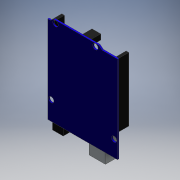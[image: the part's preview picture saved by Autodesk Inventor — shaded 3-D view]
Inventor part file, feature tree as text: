
AUTODESK INVENTOR PART (.ipt)
format: ipt  version: 2016 (Build 200138000, 138)  size: 185,856 bytes
history: native  units: mm
features: sketch x7, extrude x6, other x1
ambient origin geometry x8: Origin, YZ Plane, XZ Plane, XY Plane, X Axis, Y Axis, Z Axis, Center Point
bodies: Body1 (feature_tree)
feature tree (14):
  other  "Sólido1"
  extrude  "Extrusión1"  Depth=8.45mm TaperAngle=0.0deg
  extrude  "Extrusión2"  Depth=10.0mm TaperAngle=0.0deg
  extrude  "Extrusión3"  Depth=12.0mm TaperAngle=0.0deg
  extrude  "Extrusión4"  [1 undecoded]
  extrude  "Extrusión5"  [1 undecoded]
  extrude  "Extrusión6"  [1 undecoded]
  sketch  "Boceto7"
  sketch  "Boceto1"  dims[d25=1.0mm d26=0.0mm d39=8.45mm d40=0.0mm]
  sketch  "Boceto2"  dims[d45=8.0mm d46=0.0mm d51=10.0mm d52=0.0mm]
  sketch  "Boceto3"  dims[d57=10.0mm d58=0.0mm d60=12.0mm d61=0.0mm]
  sketch  "Boceto4"
  sketch  "Boceto5"
  sketch  "Boceto6"
note: 3 required parameter values undecoded (feature->parameter linkage not recoverable at this tier; creation-order binding heuristic only, values carry confidence <= 0.55)
